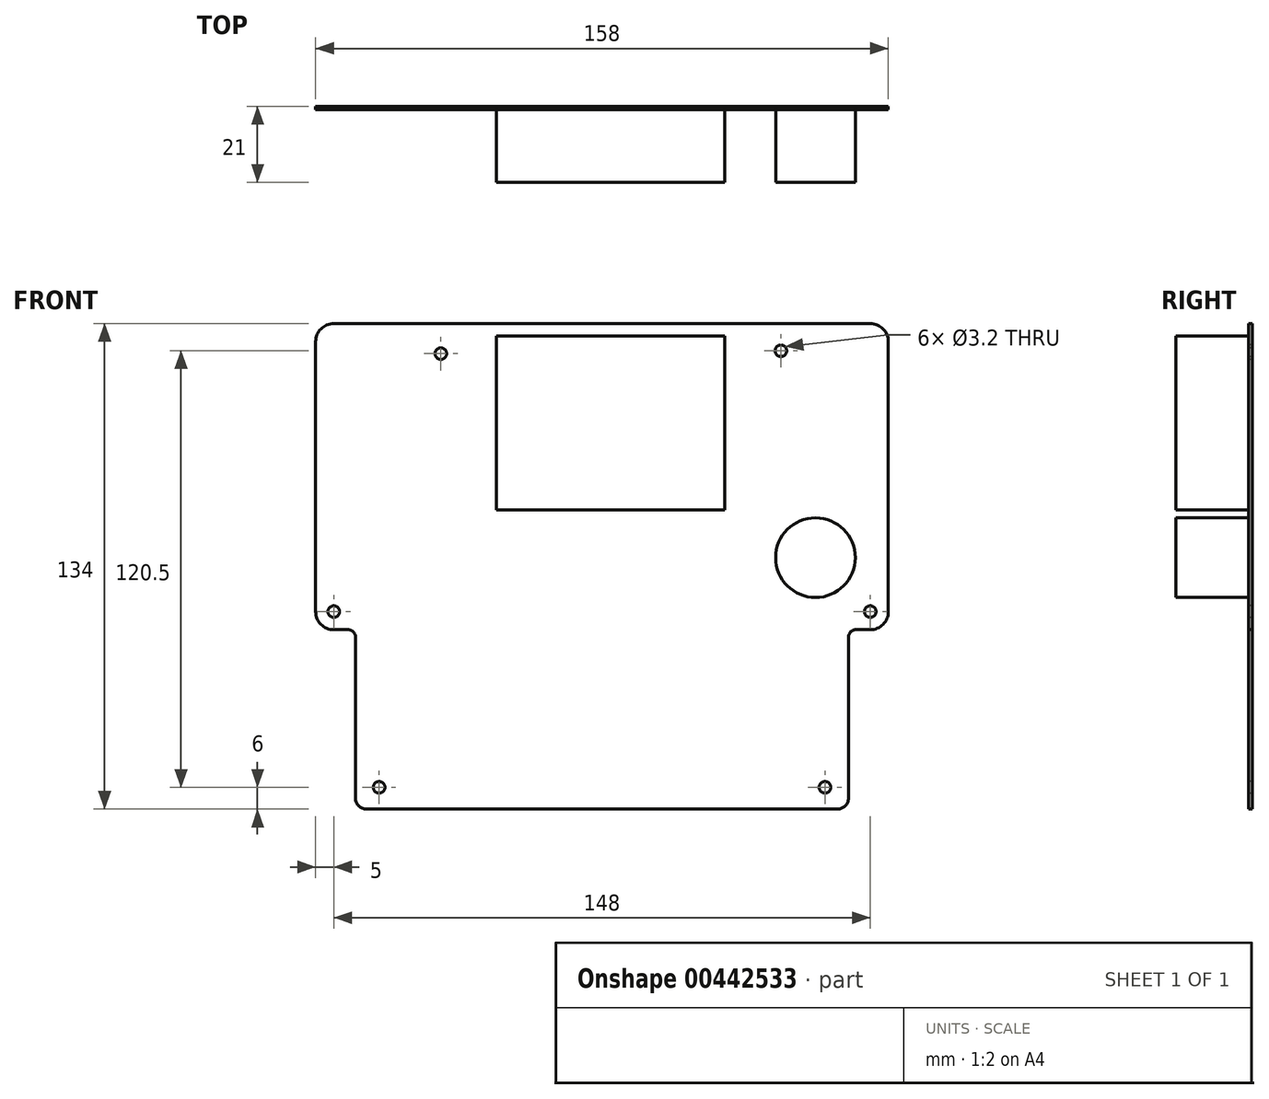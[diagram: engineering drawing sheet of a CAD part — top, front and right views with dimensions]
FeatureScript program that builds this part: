
annotation { "Feature Type Name" : "Feature", "Feature Type Description" : "" }
export const myFeature = defineFeature(function(context is Context, id is Id, definition is map)
    precondition{}
    {
        {
            var Q0;
            Q0=qCreatedBy(makeId("Front.planeOp"),FACE);
            var sketch = newSketch(context, id + "F0", { "sketchPlane" : qUnion([Q0])});
            skLineSegment(sketch, "E0", {"start": v(-79, -32) * mm, "end": v(-79, 42.5) * mm});
            skLineSegment(sketch, "E1", {"start": v(-74, 47.5) * mm, "end": v(74, 47.5) * mm});
            skLineSegment(sketch, "E2", {"start": v(79, 42.5) * mm, "end": v(79, -32) * mm});
            skLineSegment(sketch, "E3", {"start": v(74, -37) * mm, "end": v(70, -37) * mm});
            skLineSegment(sketch, "E4", {"start": v(68, -39) * mm, "end": v(68, -83.5) * mm});
            skLineSegment(sketch, "E5", {"start": v(65, -86.5) * mm, "end": v(-65, -86.5) * mm});
            skLineSegment(sketch, "E6", {"start": v(-68, -83.5) * mm, "end": v(-68, -39) * mm});
            skLineSegment(sketch, "E7", {"start": v(-70, -37) * mm, "end": v(-74, -37) * mm});
            skLineSegment(sketch, "E8", {"start": v(0, -86.5) * mm, "end": v(0, 47.5) * mm, "construction": true});
            skPoint(sketch, "E9.visualSharp", {"position": v(-79, 47.5) * mm});
            skArc(sketch, "E9.filletArc", {"start": v(-74, 47.5) * mm, "mid": v(-77.54, 46.04) * mm, "end": v(-79, 42.5) * mm});
            skPoint(sketch, "E10.visualSharp", {"position": v(79, 47.5) * mm});
            skArc(sketch, "E10.filletArc", {"start": v(79, 42.5) * mm, "mid": v(77.54, 46.04) * mm, "end": v(74, 47.5) * mm});
            skPoint(sketch, "E11.visualSharp", {"position": v(79, -37) * mm});
            skArc(sketch, "E11.filletArc", {"start": v(74, -37) * mm, "mid": v(77.54, -35.54) * mm, "end": v(79, -32) * mm});
            skPoint(sketch, "E12.visualSharp", {"position": v(-79, -37) * mm});
            skArc(sketch, "E12.filletArc", {"start": v(-79, -32) * mm, "mid": v(-77.54, -35.54) * mm, "end": v(-74, -37) * mm});
            skPoint(sketch, "E13.visualSharp", {"position": v(-68, -37) * mm});
            skArc(sketch, "E13.filletArc", {"start": v(-68, -39) * mm, "mid": v(-68.59, -37.59) * mm, "end": v(-70, -37) * mm});
            skPoint(sketch, "E14.visualSharp", {"position": v(68, -37) * mm});
            skArc(sketch, "E14.filletArc", {"start": v(70, -37) * mm, "mid": v(68.59, -37.59) * mm, "end": v(68, -39) * mm});
            skPoint(sketch, "E15.visualSharp", {"position": v(68, -86.5) * mm});
            skArc(sketch, "E15.filletArc", {"start": v(65, -86.5) * mm, "mid": v(67.12, -85.62) * mm, "end": v(68, -83.5) * mm});
            skPoint(sketch, "E16.visualSharp", {"position": v(-68, -86.5) * mm});
            skArc(sketch, "E16.filletArc", {"start": v(-68, -83.5) * mm, "mid": v(-67.12, -85.62) * mm, "end": v(-65, -86.5) * mm});
            skLineSegment(sketch, "E17.bottom", {"start": v(33.85, -3.9) * mm, "end": v(-29.15, -3.9) * mm});
            skLineSegment(sketch, "E17.top", {"start": v(33.85, 44.1) * mm, "end": v(-29.15, 44.1) * mm});
            skLineSegment(sketch, "E17.left", {"start": v(33.85, -3.9) * mm, "end": v(33.85, 44.1) * mm});
            skLineSegment(sketch, "E17.right", {"start": v(-29.15, -3.9) * mm, "end": v(-29.15, 44.1) * mm});
            skPoint(sketch, "E17.middle", {"position": v(2.35, 20.1) * mm});
            skCircle(sketch, "E18", {"center": v(58.9, -17.1) * mm, "radius": 11 * mm});
            skLineSegment(sketch, "E19", {"start": v(-68, -55) * mm, "end": v(68, -55) * mm, "construction": true});
            skLineSegment(sketch, "E20", {"start": v(68, -56) * mm, "end": v(-68, -56) * mm, "construction": true});
            skCircle(sketch, "E21", {"center": v(-74, -32) * mm, "radius": 1.6 * mm});
            skCircle(sketch, "E22", {"center": v(-61.5, -80.5) * mm, "radius": 1.6 * mm});
            skCircle(sketch, "E23", {"center": v(-44.45, 39.2) * mm, "radius": 1.6 * mm});
            skCircle(sketch, "E24", {"center": v(49.35, 40) * mm, "radius": 1.6 * mm});
            skLineSegment(sketch, "E25", {"start": v(-79, 0) * mm, "end": v(79, 0) * mm, "construction": true});
            skCircle(sketch, "E26.MirrorC", {"center": v(61.5, -80.5) * mm, "radius": 1.6 * mm});
            skCircle(sketch, "E27.MirrorC", {"center": v(74, -32) * mm, "radius": 1.6 * mm});
            skSolve(sketch);
        }
        {
            var Q0;
            Q0=makeQuery(id+"F0.imprint","IMPRINT",FACE,{"disambiguationData":[TD([[makeQuery(id+"F0.imprint","IMPRINT",EDGE,{"derivedFrom":sQuery(id+"F0.wireOp",EDGE,"E0")}),-1.0]])]});
            var Q1;
            Q1=makeQuery(id+"F0.imprint","IMPRINT",FACE,{"disambiguationData":[TD([[makeQuery(id+"F0.imprint","IMPRINT",EDGE,{"derivedFrom":sQuery(id+"F0.wireOp",EDGE,"E17.bottom")}),-1.0]])]});
            var Q2;
            Q2=makeQuery(id+"F0.imprint","IMPRINT",FACE,{"disambiguationData":[TD([[makeQuery(id+"F0.imprint","IMPRINT",EDGE,{"derivedFrom":sQuery(id+"F0.wireOp",EDGE,"E18")}),1.0]])]});
            extrude(context, id + "F1", {"entities" : qUnion([Q0, Q1, Q2]), "oppositeDirection" : true, "depth" : 1 * mm});
        }
        {
            var Q0;
            Q0=makeQuery(id+"F0.imprint","IMPRINT",FACE,{"disambiguationData":[TD([[makeQuery(id+"F0.imprint","IMPRINT",EDGE,{"derivedFrom":sQuery(id+"F0.wireOp",EDGE,"E17.bottom")}),-1.0]])]});
            var Q1;
            Q1=makeQuery(id+"F0.imprint","IMPRINT",FACE,{"disambiguationData":[TD([[makeQuery(id+"F0.imprint","IMPRINT",EDGE,{"derivedFrom":sQuery(id+"F0.wireOp",EDGE,"E18")}),1.0]])]});
            extrude(context, id + "F2", {"entities" : qUnion([Q0, Q1]), "operationType" : NewBodyOperationType.ADD, "depth" : 20 * mm});
        }
    });
